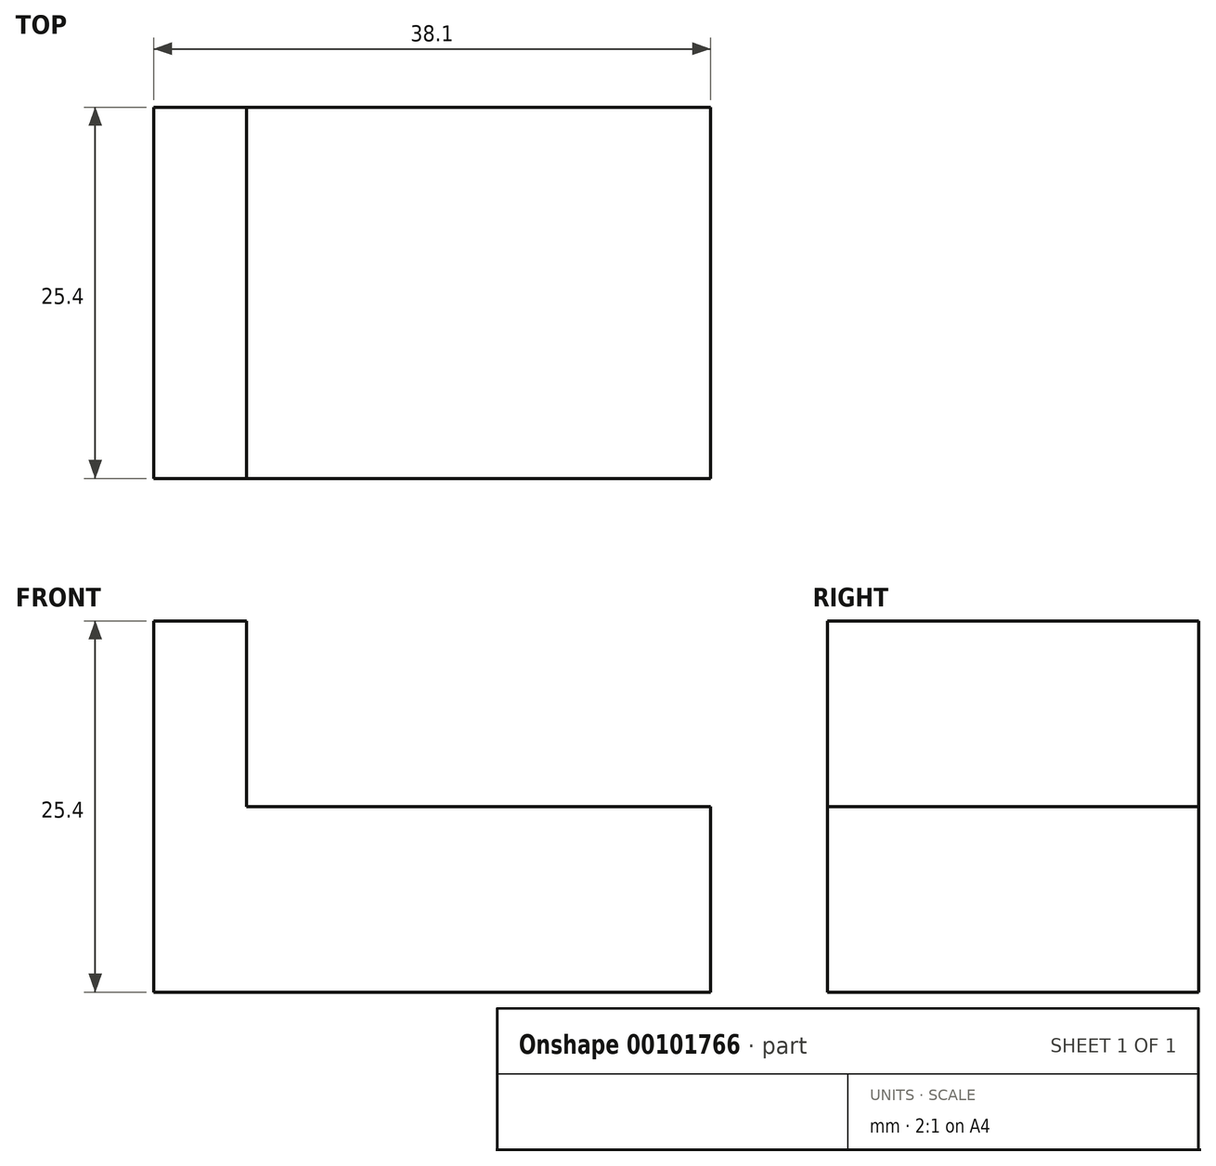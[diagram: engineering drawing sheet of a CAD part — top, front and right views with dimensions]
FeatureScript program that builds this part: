
annotation { "Feature Type Name" : "Feature", "Feature Type Description" : "" }
export const myFeature = defineFeature(function(context is Context, id is Id, definition is map)
    precondition{}
    {
        {
            var Q0;
            Q0=qCreatedBy(makeId("Front.planeOp"),FACE);
            var sketch = newSketch(context, id + "F0", { "sketchPlane" : qUnion([Q0])});
            skLineSegment(sketch, "E0", {"start": v(0, 0) * mm, "end": v(0, 25.4) * mm});
            skLineSegment(sketch, "E1", {"start": v(0, 25.4) * mm, "end": v(6.35, 25.4) * mm});
            skLineSegment(sketch, "E2", {"start": v(6.35, 25.4) * mm, "end": v(6.35, 12.7) * mm});
            skLineSegment(sketch, "E3", {"start": v(6.35, 12.7) * mm, "end": v(38.1, 12.7) * mm});
            skLineSegment(sketch, "E4", {"start": v(38.1, 12.7) * mm, "end": v(38.1, 0) * mm});
            skLineSegment(sketch, "E5", {"start": v(38.1, 0) * mm, "end": v(0, 0) * mm});
            skSolve(sketch);
        }
        {
            var Q0;
            Q0 = qSketchRegion(id + "F0", true);
            extrude(context, id + "F1", {"entities" : qUnion([Q0]), "depth" : 25.4 * mm});
        }
    });
